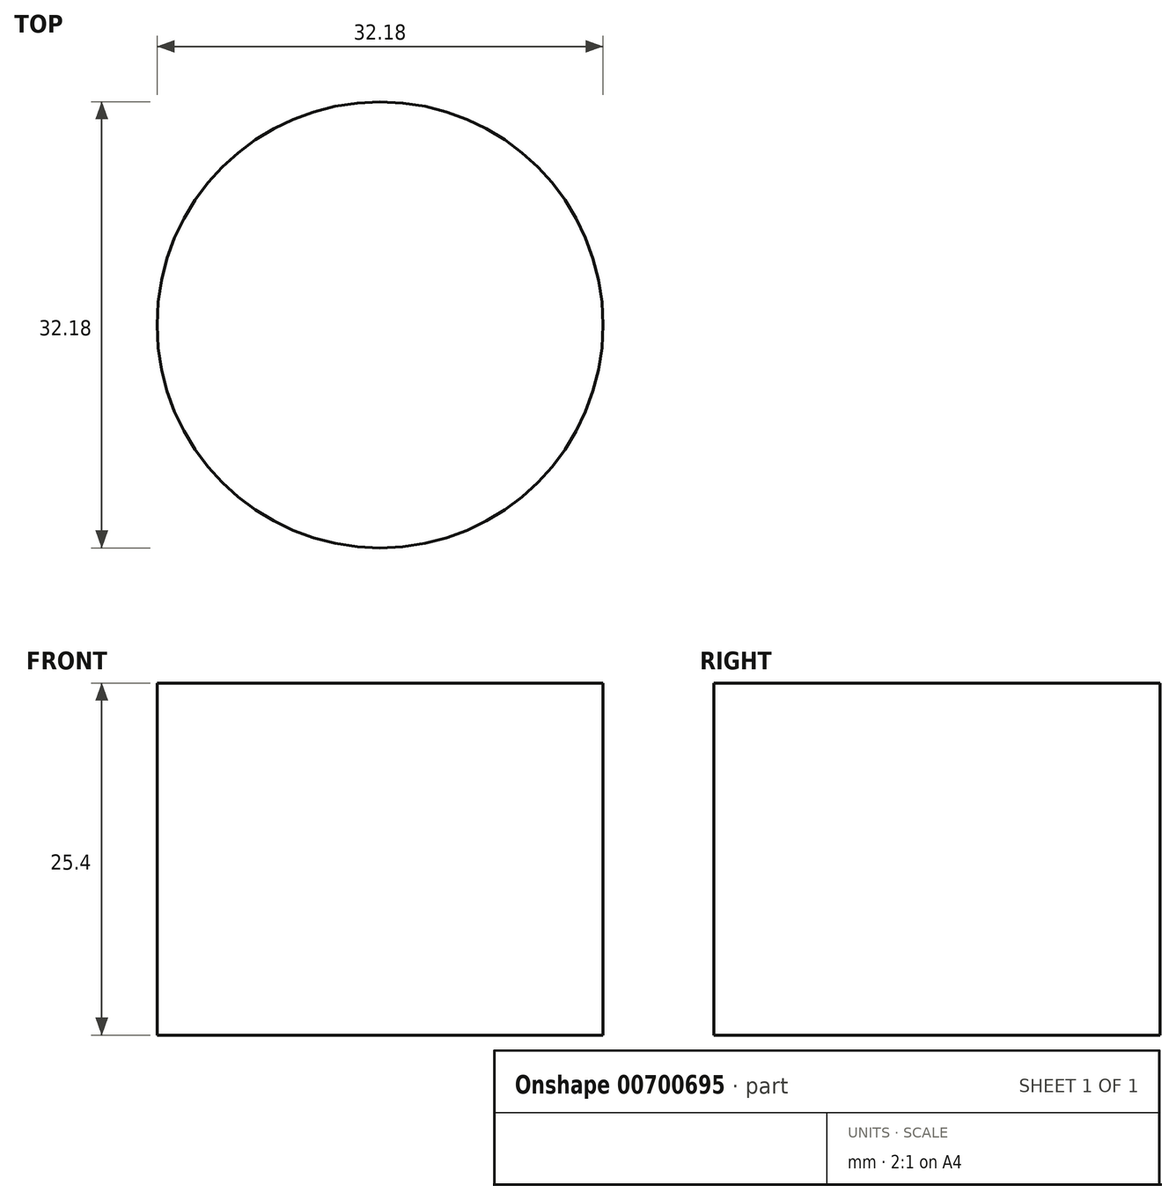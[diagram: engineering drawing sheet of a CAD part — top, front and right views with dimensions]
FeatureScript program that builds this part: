
annotation { "Feature Type Name" : "Feature", "Feature Type Description" : "" }
export const myFeature = defineFeature(function(context is Context, id is Id, definition is map)
    precondition{}
    {
        {
            var Q0;
            Q0=qCreatedBy(makeId("Top.planeOp"),FACE);
            var sketch = newSketch(context, id + "F0", { "sketchPlane" : qUnion([Q0])});
            skCircle(sketch, "E0", {"center": v(-34.8, 0) * mm, "radius": 16.1 * mm});
            skSolve(sketch);
        }
        {
            var Q0;
            Q0=makeQuery(id+"F0.imprint","IMPRINT",FACE,{"disambiguationData":[TD([[makeQuery(id+"F0.imprint","IMPRINT",EDGE,{"derivedFrom":sQuery(id+"F0.wireOp",EDGE,"E0")}),1.0]])]});
            extrude(context, id + "F1", {"entities" : qUnion([Q0]), "depth" : 25.4 * mm, "offsetDistance" : 25.4 * mm});
        }
    });
